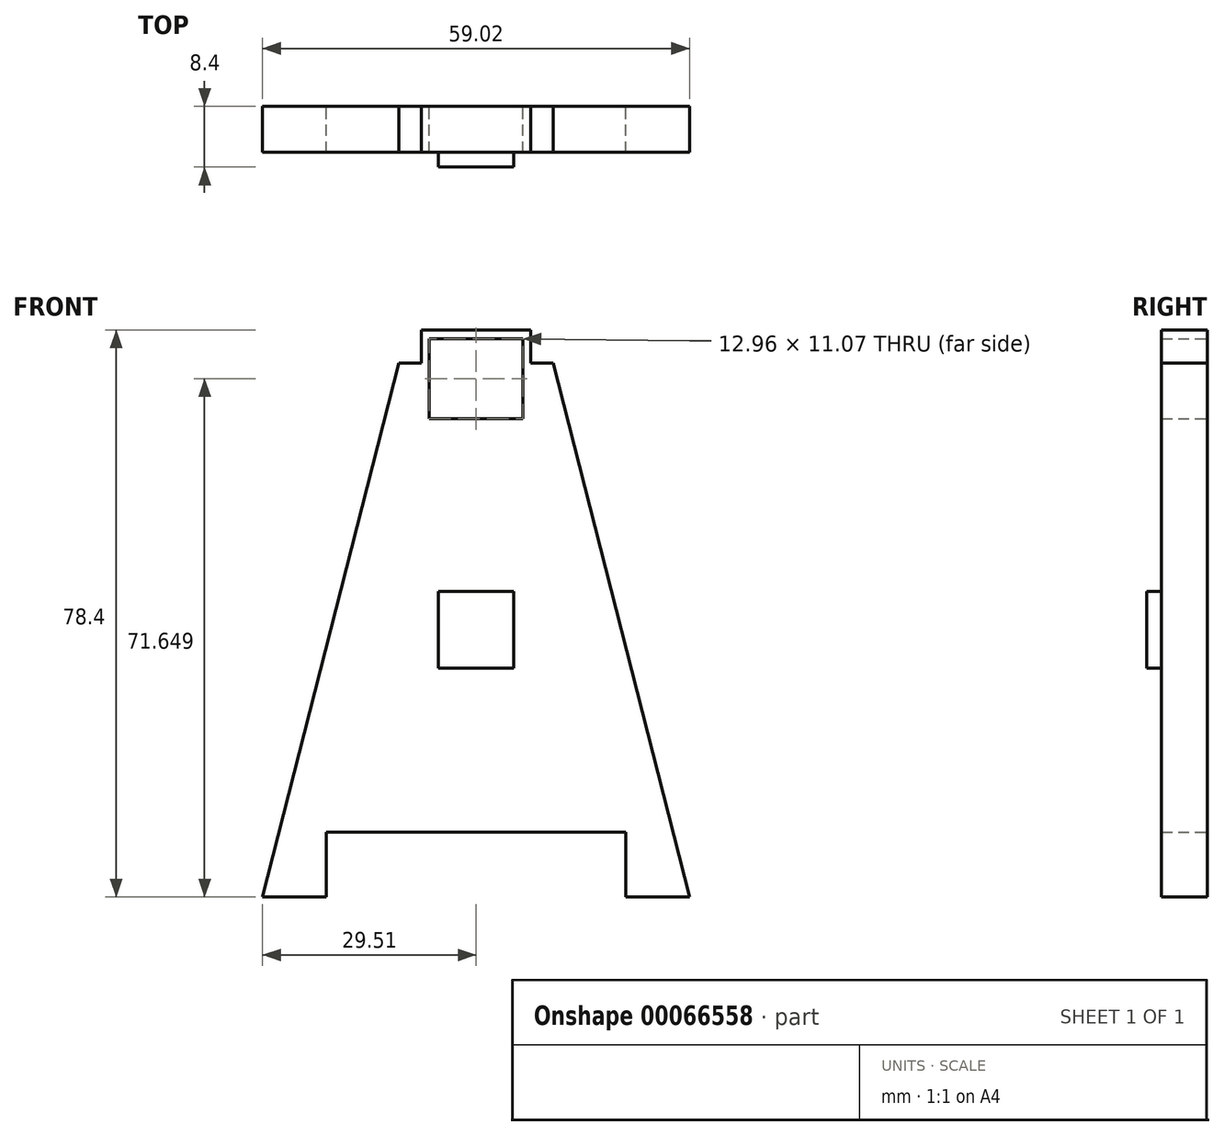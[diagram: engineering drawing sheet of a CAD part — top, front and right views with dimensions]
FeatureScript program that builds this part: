
annotation { "Feature Type Name" : "Feature", "Feature Type Description" : "" }
export const myFeature = defineFeature(function(context is Context, id is Id, definition is map)
    precondition{}
    {
        {
            var Q0;
            Q0=qCreatedBy(makeId("Front.planeOp"),FACE);
            var sketch = newSketch(context, id + "F0", { "sketchPlane" : qUnion([Q0])});
            skLineSegment(sketch, "E0", {"start": v(-10.67, 37.23) * mm, "end": v(-29.51, -36.6) * mm});
            skLineSegment(sketch, "E1", {"start": v(-29.51, -36.6) * mm, "end": v(-20.72, -36.6) * mm});
            skLineSegment(sketch, "E2", {"start": v(-20.72, -36.6) * mm, "end": v(-20.72, -27.65) * mm});
            skLineSegment(sketch, "E3", {"start": v(-20.72, -27.65) * mm, "end": v(0, -27.65) * mm});
            skLineSegment(sketch, "E4", {"start": v(-7.57, 37.23) * mm, "end": v(-7.57, 29.5) * mm});
            skLineSegment(sketch, "E5", {"start": v(-7.57, 29.5) * mm, "end": v(0, 29.5) * mm});
            skLineSegment(sketch, "E6.MirrorCS", {"start": v(7.57, 29.5) * mm, "end": v(0, 29.5) * mm});
            skLineSegment(sketch, "E7.MirrorCS", {"start": v(7.57, 37.23) * mm, "end": v(7.57, 29.5) * mm});
            skLineSegment(sketch, "E8.MirrorCS", {"start": v(10.67, 37.23) * mm, "end": v(29.51, -36.6) * mm});
            skLineSegment(sketch, "E9.MirrorCS", {"start": v(29.51, -36.6) * mm, "end": v(20.72, -36.6) * mm});
            skLineSegment(sketch, "E10.MirrorCS", {"start": v(20.72, -27.65) * mm, "end": v(0, -27.65) * mm});
            skLineSegment(sketch, "E11.MirrorCS", {"start": v(20.72, -36.6) * mm, "end": v(20.72, -27.65) * mm});
            skLineSegment(sketch, "E12", {"start": v(-7.57, 37.23) * mm, "end": v(-7.57, 41.8) * mm});
            skLineSegment(sketch, "E13", {"start": v(-7.57, 41.8) * mm, "end": v(0, 41.8) * mm});
            skLineSegment(sketch, "E14.MirrorCS", {"start": v(7.57, 41.8) * mm, "end": v(0, 41.8) * mm});
            skLineSegment(sketch, "E15.MirrorCS", {"start": v(7.57, 37.23) * mm, "end": v(7.57, 41.8) * mm});
            skLineSegment(sketch, "E16", {"start": v(-6.48, 29.5) * mm, "end": v(-6.48, 40.58) * mm});
            skLineSegment(sketch, "E17", {"start": v(-6.48, 40.58) * mm, "end": v(0, 40.58) * mm});
            skLineSegment(sketch, "E18.MirrorCS", {"start": v(6.48, 40.58) * mm, "end": v(0, 40.58) * mm});
            skLineSegment(sketch, "E19.MirrorCS", {"start": v(6.48, 29.5) * mm, "end": v(6.48, 40.58) * mm});
            skLineSegment(sketch, "E20", {"start": v(-10.67, 37.23) * mm, "end": v(10.67, 37.23) * mm});
            skSolve(sketch);
        }
        {
            var Q0;
            Q0 = qSketchRegion(id + "F0", true);
            extrude(context, id + "F1", {"entities" : qUnion([Q0]), "depth" : 6.35 * mm});
        }
        {
            var Q0;
            Q0=qCreatedBy(makeId("Front.planeOp"),FACE);
            var sketch = newSketch(context, id + "F2", { "sketchPlane" : qUnion([Q0])});
            skLineSegment(sketch, "E21", {"start": v(-5.22, 5.64) * mm, "end": v(-5.22, -4.99) * mm});
            skLineSegment(sketch, "E22", {"start": v(-5.22, -4.99) * mm, "end": v(0, -4.99) * mm});
            skLineSegment(sketch, "E23", {"start": v(-5.22, 5.64) * mm, "end": v(0, 5.64) * mm});
            skLineSegment(sketch, "E24.MirrorCS", {"start": v(5.22, 5.64) * mm, "end": v(0, 5.64) * mm});
            skLineSegment(sketch, "E25.MirrorCS", {"start": v(5.22, 5.64) * mm, "end": v(5.22, -4.99) * mm});
            skLineSegment(sketch, "E26.MirrorCS", {"start": v(5.22, -4.99) * mm, "end": v(0, -4.99) * mm});
            skSolve(sketch);
        }
        {
            var Q0;
            Q0 = qSketchRegion(id + "F2", true);
            extrude(context, id + "F3", {"entities" : qUnion([Q0]), "operationType" : NewBodyOperationType.ADD, "depth" : 8.4 * mm});
        }
    });
